# Revit family: Tub_Spout-DXV-Fitzgerald-D35160760_Series
name_source: partatom
category: Plumbing Fixtures
revit_build: Autodesk Revit 2014 (Build: 20130308_1515(x64)
units: mm (PartAtom-declared; Revit-internal decimal feet)

## types (3) — shared parameters
ADA Compliant = Yes
Assembly Code = D2010710
CW Connection = Yes
CWFU = 3
Default Elevation = 21"
Description = Fitzgerald Wall Tub Spout
HW Connection = Yes
HWFU = 3
Height = 2 5/8"
Installation Type = Wall Mounted
Length = 8"
Manufacturer = DXV
Price = Prices may vary. Please consult Manufacturer Representative for most up-to-date price list.
Product Documentation Link = https://dxv01.blob.core.windows.net
Product Page URL = https://www.dxv.com
Tempered Water Connection Diameter = 1/2"
URL = http://www.dxv.com
Vent Connection = No
WFU = 4
Warranty Documentation Link = https://www.dxv.com
Waste Connection = No
Width = 2 5/8"

## per-type parameters (varying)
| type | Finish | Material |
| D35160760.100 | Cast Brass-DXV-100-Polished Chrome | Cast Brass-DXV-100-Polished Chrome |
| D35160760.144 | Cast Brass-DXV-144-Brushed Nickel | Cast Brass-DXV-144-Brushed Nickel |
| D35160760.150 | Cast Brass-DXV-150-Platinum Nickel | Cast Brass-DXV-150-Platinum Nickel |

note: column(s) folded — value = type name in every type: Model

## geometry (parser evidence)
native form markers: Sweep x3
no freeform markers — native parametric forms only
